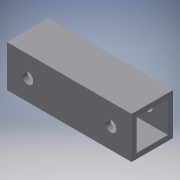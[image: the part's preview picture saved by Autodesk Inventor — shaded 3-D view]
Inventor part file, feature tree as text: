
AUTODESK INVENTOR PART (.ipt)
format: ipt  version: 2016 (Build 200138000, 138)  size: 113,152 bytes
history: native  units: in
note: dims shown in document units (in); Inventor stores cm internally (conversion verified against a paired STEP export)
features: extrude x2, sketch x2
ambient origin geometry x8: Origin, YZ Plane, XZ Plane, XY Plane, X Axis, Y Axis, Z Axis, Center Point
bodies: Solid1 (feature_tree)
feature tree (4):
  extrude  "Extrusion1"  Depth=1.0in
  extrude  "Extrusion2"  Depth=3.375in TaperAngle=0.0deg
  sketch  "Sketch1"  dims[d0=1.0in d1=1.0in]
  sketch  "Sketch2"  dims[d2=0.125in d3=3.375in d4=0.0in d5=0.2656in d6=0.2656in d7=0.5in d8=0.5in d9=0.5in d10=0.5in d11=1.0in d12=0.0in d13=0.2656in d14=1.0in d15=0.5in]
